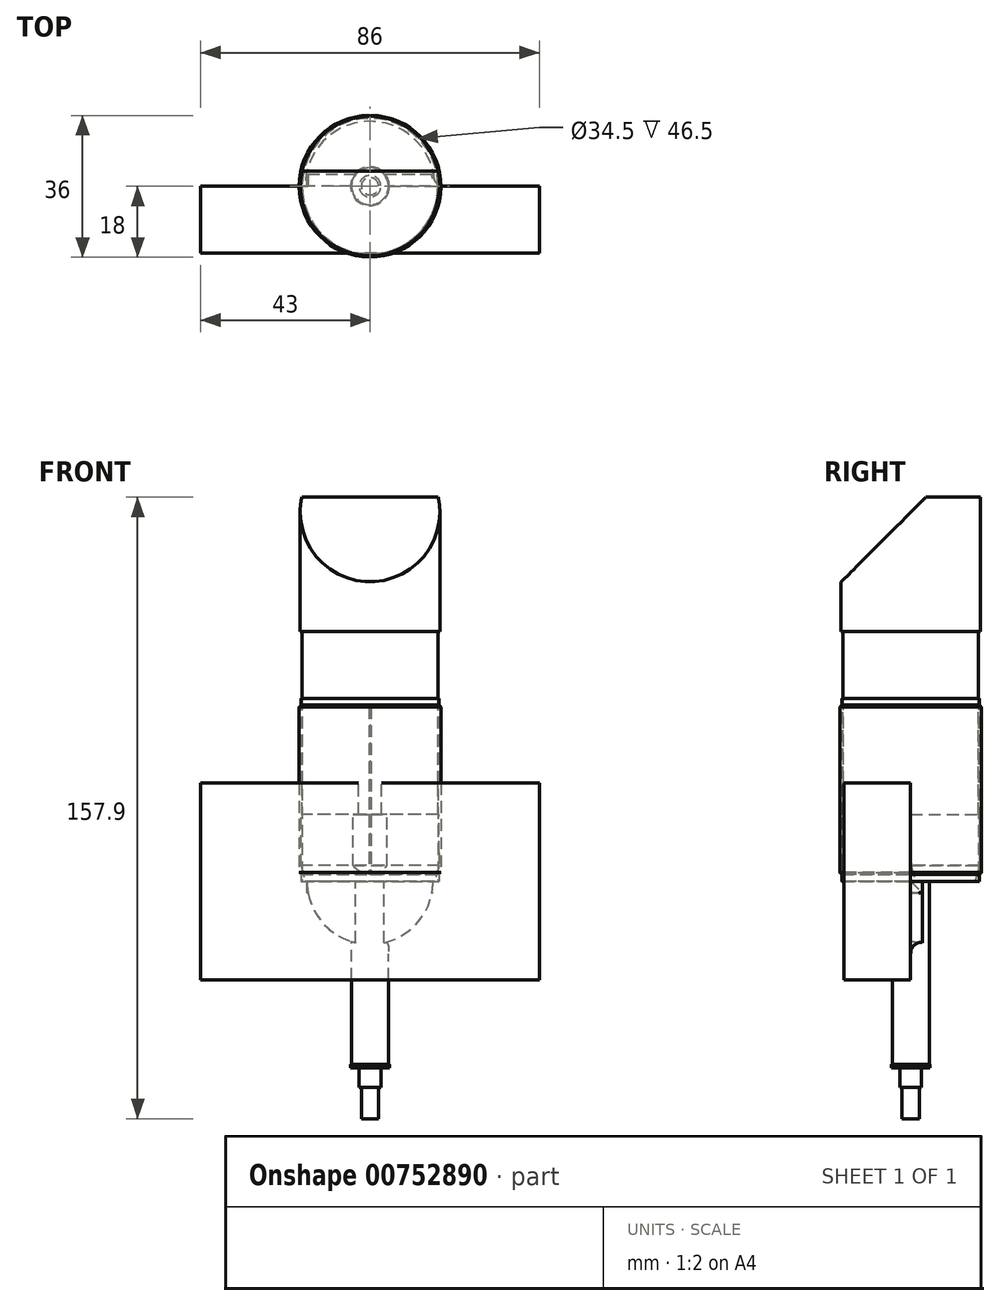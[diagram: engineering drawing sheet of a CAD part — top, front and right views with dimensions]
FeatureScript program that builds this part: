
annotation { "Feature Type Name" : "Feature", "Feature Type Description" : "" }
export const myFeature = defineFeature(function(context is Context, id is Id, definition is map)
    precondition{}
    {
        {
            var Q0;
            Q0=qCreatedBy(makeId("Front.planeOp"),FACE);
            var sketch = newSketch(context, id + "F0", { "sketchPlane" : qUnion([Q0])});
            skLineSegment(sketch, "E0.bottom", {"start": v(-4.7, 46.5) * mm, "end": v(4.7, 46.5) * mm, "construction": true});
            skLineSegment(sketch, "E0.top", {"start": v(-4.7, -46.5) * mm, "end": v(4.7, -46.5) * mm, "construction": true});
            skLineSegment(sketch, "E0.left", {"start": v(-4.7, 46.5) * mm, "end": v(-4.7, -46.5) * mm});
            skLineSegment(sketch, "E0.right", {"start": v(4.7, 46.5) * mm, "end": v(4.7, -46.5) * mm});
            skPoint(sketch, "E0.middle", {"position": v(0, 0) * mm});
            skLineSegment(sketch, "E1", {"start": v(-4.7, -46.5) * mm, "end": v(-4.92, -46.5) * mm});
            skLineSegment(sketch, "E2", {"start": v(-4.92, -46.5) * mm, "end": v(-4.92, -47.4) * mm});
            skLineSegment(sketch, "E3", {"start": v(-4.92, -47.4) * mm, "end": v(-2.75, -47.4) * mm});
            skLineSegment(sketch, "E4", {"start": v(0, 54.2) * mm, "end": v(0, -60.3) * mm});
            skLineSegment(sketch, "E5", {"start": v(-2.75, -47.4) * mm, "end": v(-2.75, -52.3) * mm});
            skLineSegment(sketch, "E6", {"start": v(-2.75, -52.3) * mm, "end": v(-2.2, -52.3) * mm});
            skLineSegment(sketch, "E7", {"start": v(-2.2, -52.3) * mm, "end": v(-2.2, -60.3) * mm});
            skLineSegment(sketch, "E8", {"start": v(-2.2, -60.3) * mm, "end": v(0, -60.3) * mm});
            skLineSegment(sketch, "E9.MirrorCS", {"start": v(2.2, -60.3) * mm, "end": v(0, -60.3) * mm});
            skLineSegment(sketch, "E10.MirrorCS", {"start": v(2.2, -52.3) * mm, "end": v(2.2, -60.3) * mm});
            skLineSegment(sketch, "E11.MirrorCS", {"start": v(2.75, -52.3) * mm, "end": v(2.2, -52.3) * mm});
            skLineSegment(sketch, "E12.MirrorCS", {"start": v(2.75, -47.4) * mm, "end": v(2.75, -52.3) * mm});
            skLineSegment(sketch, "E13.MirrorCS", {"start": v(4.93, -47.4) * mm, "end": v(2.75, -47.4) * mm});
            skLineSegment(sketch, "E14.MirrorCS", {"start": v(4.93, -46.5) * mm, "end": v(4.93, -47.4) * mm});
            skLineSegment(sketch, "E15.MirrorCS", {"start": v(4.7, -46.5) * mm, "end": v(4.93, -46.5) * mm});
            skLineSegment(sketch, "E16", {"start": v(-4.7, 46.5) * mm, "end": v(-4.92, 46.5) * mm});
            skLineSegment(sketch, "E17", {"start": v(-4.92, 46.5) * mm, "end": v(-4.92, 47.4) * mm});
            skLineSegment(sketch, "E18", {"start": v(-4.92, 47.4) * mm, "end": v(-2.4, 47.4) * mm});
            skLineSegment(sketch, "E19", {"start": v(-2.4, 47.4) * mm, "end": v(-2.4, 54.2) * mm});
            skLineSegment(sketch, "E20", {"start": v(-2.4, 54.2) * mm, "end": v(0, 54.2) * mm});
            skLineSegment(sketch, "E21.MirrorCS", {"start": v(2.4, 54.2) * mm, "end": v(0, 54.2) * mm});
            skLineSegment(sketch, "E22.MirrorCS", {"start": v(2.4, 47.4) * mm, "end": v(2.4, 54.2) * mm});
            skLineSegment(sketch, "E23.MirrorCS", {"start": v(4.92, 47.4) * mm, "end": v(2.4, 47.4) * mm});
            skLineSegment(sketch, "E24.MirrorCS", {"start": v(4.93, 46.5) * mm, "end": v(4.93, 47.4) * mm});
            skLineSegment(sketch, "E25.MirrorCS", {"start": v(4.7, 46.5) * mm, "end": v(4.92, 46.5) * mm});
            skSolve(sketch);
        }
        {
            var Q0;
            Q0=makeQuery(id+"F0.imprint","IMPRINT",FACE,{"disambiguationData":[TD([[makeQuery(id+"F0.imprint","IMPRINT",EDGE,{"derivedFrom":sQuery(id+"F0.wireOp",EDGE,"E0.left")}),1.0]])]});
            var Q1;
            Q1=sQuery(id+"F0.wireOp",EDGE,"E4");
            revolve(context, id + "F1", {"surfaceOperationType" : NewSurfaceOperationType.NEW, "entities" : qUnion([Q0]), "axis" : qUnion([Q1]), "revolveType" : RevolveType.FULL});
        }
        {
            var Q0;
            Q0=qCreatedBy(makeId("Front.planeOp"),FACE);
            var sketch = newSketch(context, id + "F2", { "sketchPlane" : qUnion([Q0])});
            skLineSegment(sketch, "E26", {"start": v(0, 0) * mm, "end": v(16.5, 0) * mm});
            skLineSegment(sketch, "E27", {"start": v(16.5, 0) * mm, "end": v(17.55, 4) * mm});
            skLineSegment(sketch, "E28", {"start": v(17.55, 4) * mm, "end": v(17.55, 17) * mm});
            skLineSegment(sketch, "E29", {"start": v(17.55, 17) * mm, "end": v(17.25, 17) * mm});
            skLineSegment(sketch, "E30", {"start": v(17.25, 17) * mm, "end": v(17.25, 63.5) * mm});
            skLineSegment(sketch, "E31", {"start": v(17.25, 63.5) * mm, "end": v(17.75, 63.5) * mm});
            skLineSegment(sketch, "E32", {"start": v(17.75, 63.5) * mm, "end": v(17.75, 97.6) * mm});
            skLineSegment(sketch, "E33", {"start": v(17.75, 97.6) * mm, "end": v(0, 97.6) * mm});
            skLineSegment(sketch, "E34", {"start": v(0, 97.6) * mm, "end": v(0, 0) * mm});
            skSolve(sketch);
        }
        {
            var Q0;
            Q0=makeQuery(id+"F2.imprint","IMPRINT",FACE,{"disambiguationData":[TD([[makeQuery(id+"F2.imprint","IMPRINT",EDGE,{"derivedFrom":sQuery(id+"F2.wireOp",EDGE,"E26")}),1.0]])]});
            var Q1;
            Q1=sQuery(id+"F2.wireOp",EDGE,"E34");
            revolve(context, id + "F3", {"surfaceOperationType" : NewSurfaceOperationType.NEW, "entities" : qUnion([Q0]), "axis" : qUnion([Q1]), "revolveType" : RevolveType.FULL});
        }
        {
            var Q0;
            Q0=qCreatedBy(makeId("Right.planeOp"),FACE);
            var sketch = newSketch(context, id + "F4", { "sketchPlane" : qUnion([Q0])});
            skLineSegment(sketch, "E35", {"start": v(-17.75, 63.5) * mm, "end": v(-17.75, 97.6) * mm, "construction": true});
            skLineSegment(sketch, "E36.0", {"start": v(-17.75, 97.6) * mm, "end": v(17.75, 97.6) * mm, "construction": true});
            skLineSegment(sketch, "E37", {"start": v(17.75, 97.6) * mm, "end": v(17.75, 63.5) * mm, "construction": true});
            skLineSegment(sketch, "E38.0", {"start": v(-17.75, 63.5) * mm, "end": v(17.75, 63.5) * mm, "construction": true});
            skLineSegment(sketch, "E39", {"start": v(-17.75, 97.6) * mm, "end": v(3.85, 97.6) * mm});
            skLineSegment(sketch, "E40", {"start": v(3.85, 97.6) * mm, "end": v(-17.75, 76) * mm});
            skLineSegment(sketch, "E41", {"start": v(-17.75, 76) * mm, "end": v(-17.75, 97.6) * mm});
            skLineSegment(sketch, "E42.0", {"start": v(-16.5, 0) * mm, "end": v(16.5, 0) * mm, "construction": true});
            skSolve(sketch);
        }
        {
            var Q0;
            Q0=makeQuery(id+"F4.imprint","IMPRINT",FACE,{"disambiguationData":[TD([[makeQuery(id+"F4.imprint","IMPRINT",EDGE,{"derivedFrom":sQuery(id+"F4.wireOp",EDGE,"E39")}),-1.0]])]});
            extrude(context, id + "F5", {"entities" : qUnion([Q0]), "operationType" : NewBodyOperationType.REMOVE, "endBound" : BoundingType.SYMMETRIC, "oppositeDirection" : true, "depth" : 50 * mm, "offsetDistance" : 25 * mm});
        }
        {
            var Q0;
            Q0=qCreatedBy(makeId("Front.planeOp"),FACE);
            var sketch = newSketch(context, id + "F6", { "sketchPlane" : qUnion([Q0])});
            skLineSegment(sketch, "E43", {"start": v(17.25, 46.5) * mm, "end": v(17.25, 0) * mm});
            skLineSegment(sketch, "E44", {"start": v(17.25, 0) * mm, "end": v(17.5, 0) * mm});
            skLineSegment(sketch, "E45", {"start": v(17.5, 0) * mm, "end": v(17.5, 1.75) * mm});
            skLineSegment(sketch, "E46", {"start": v(17.5, 1.75) * mm, "end": v(18, 1.75) * mm});
            skLineSegment(sketch, "E47", {"start": v(18, 1.75) * mm, "end": v(18, 44.75) * mm});
            skLineSegment(sketch, "E48", {"start": v(18, 44.75) * mm, "end": v(17.5, 44.75) * mm});
            skLineSegment(sketch, "E49", {"start": v(17.5, 44.75) * mm, "end": v(17.5, 46.5) * mm});
            skLineSegment(sketch, "E50", {"start": v(17.5, 46.5) * mm, "end": v(17.25, 46.5) * mm});
            skLineSegment(sketch, "E51", {"start": v(0, 1.24) * mm, "end": v(0, 39.4) * mm, "construction": true});
            skSolve(sketch);
        }
        {
            var Q0;
            Q0=makeQuery(id+"F6.imprint","IMPRINT",FACE,{"disambiguationData":[TD([[makeQuery(id+"F6.imprint","IMPRINT",EDGE,{"derivedFrom":sQuery(id+"F6.wireOp",EDGE,"E43")}),1.0]])]});
            var Q1;
            Q1=sQuery(id+"F6.wireOp",EDGE,"E51");
            revolve(context, id + "F7", {"surfaceOperationType" : NewSurfaceOperationType.NEW, "entities" : qUnion([Q0]), "axis" : qUnion([Q1]), "revolveType" : RevolveType.FULL});
        }
        {
            var Q0;
            Q0=makeQuery(id+"F7.opRevolve","SWEPT_EDGE",EDGE,{"disambiguationData":[OSD([sQuery(id+"F6.wireOp",EDGE,"E47"),sQuery(id+"F6.wireOp",EDGE,"E48")])]});
            var Q1;
            Q1=makeQuery(id+"F7.opRevolve","SWEPT_EDGE",EDGE,{"disambiguationData":[OSD([sQuery(id+"F6.wireOp",EDGE,"E46"),sQuery(id+"F6.wireOp",EDGE,"E47")])]});
            chamfer(context, id + "F8", {"entities" : qUnion([Q0, Q1]), "width" : 0.5 * mm, "tangentPropagation" : true});
        }
        {
            var Q0;
            Q0=qCreatedBy(makeId("Top.planeOp"),FACE);
            var sketch = newSketch(context, id + "F9", { "sketchPlane" : qUnion([Q0])});
            skLineSegment(sketch, "E52", {"start": v(0, 17.8) * mm, "end": v(-0.2, 18) * mm});
            skLineSegment(sketch, "E53", {"start": v(-0.2, 18) * mm, "end": v(0, 18) * mm});
            skLineSegment(sketch, "E54.MirrorCS", {"start": v(0.2, 18) * mm, "end": v(0, 18) * mm});
            skLineSegment(sketch, "E55.MirrorCS", {"start": v(0, 17.8) * mm, "end": v(0.2, 18) * mm});
            skCircle(sketch, "E56.0", {"center": v(0, 0) * mm, "radius": 18 * mm, "construction": true});
            skSolve(sketch);
        }
        {
            var Q0;
            Q0=makeQuery(id+"F9.imprint","IMPRINT",FACE,{"disambiguationData":[TD([[makeQuery(id+"F9.imprint","IMPRINT",EDGE,{"derivedFrom":sQuery(id+"F9.wireOp",EDGE,"E52")}),-1.0]])]});
            var Q1;
            Q1=makeQuery(id+"F7.opRevolve","SWEPT_FACE",FACE,{"disambiguationData":[OSD([sQuery(id+"F6.wireOp",EDGE,"E48")])]});
            extrude(context, id + "F10", {"entities" : qUnion([Q0]), "operationType" : NewBodyOperationType.REMOVE, "endBound" : BoundingType.THROUGH_ALL, "depth" : 25 * mm, "endBoundEntityFace" : qUnion([Q1]), "offsetDistance" : 25 * mm});
        }
        {
            var Q0;
            Q0=qCreatedBy(makeId("Front.planeOp"),FACE);
            var sketch = newSketch(context, id + "F11", { "sketchPlane" : qUnion([Q0])});
            skLineSegment(sketch, "E57.bottom", {"start": v(43, 25) * mm, "end": v(-43, 25) * mm});
            skLineSegment(sketch, "E57.top", {"start": v(43, -25) * mm, "end": v(-43, -25) * mm});
            skLineSegment(sketch, "E57.left", {"start": v(43, 25) * mm, "end": v(43, -25) * mm});
            skLineSegment(sketch, "E57.right", {"start": v(-43, 25) * mm, "end": v(-43, -25) * mm});
            skPoint(sketch, "E57.middle", {"position": v(0, 0) * mm});
            skSolve(sketch);
        }
        {
            var Q0;
            Q0=makeQuery(id+"F11.imprint","IMPRINT",FACE,{"disambiguationData":[TD([[makeQuery(id+"F11.imprint","IMPRINT",EDGE,{"derivedFrom":sQuery(id+"F11.wireOp",EDGE,"E57.bottom")}),1.0]])]});
            extrude(context, id + "F12", {"entities" : qUnion([Q0]), "depth" : 17 * mm, "offsetDistance" : 25 * mm});
        }
        {
            var Q0;
            Q0=makeQuery(id+"F12.opExtrude","CAP_FACE",FACE,{"disambiguationData":[OSD([sQuery(id+"F11.wireOp",EDGE,"E57.bottom"),sQuery(id+"F11.wireOp",EDGE,"E57.top"),sQuery(id+"F11.wireOp",EDGE,"E57.left"),sQuery(id+"F11.wireOp",EDGE,"E57.right")])],"isStart":true});
            var sketch = newSketch(context, id + "F13", { "sketchPlane" : qUnion([Q0])});
            skCircle(sketch, "E58", {"center": v(0, 0) * mm, "radius": 16 * mm});
            skSolve(sketch);
        }
        {
            var Q0;
            Q0=makeQuery(id+"F13.imprint","IMPRINT",FACE,{"disambiguationData":[TD([[makeQuery(id+"F13.imprint","IMPRINT",EDGE,{"derivedFrom":sQuery(id+"F13.wireOp",EDGE,"E58")}),1.0]])]});
            extrude(context, id + "F14", {"entities" : qUnion([Q0]), "operationType" : NewBodyOperationType.ADD, "depth" : 3 * mm, "offsetDistance" : 25 * mm});
        }
        {
            var Q0;
            Q0=makeQuery(id+"F14.opExtrude","CAP_EDGE",EDGE,{"disambiguationData":[OSD([sQuery(id+"F13.wireOp",EDGE,"E58")])],"isStart":true});
            fillet(context, id + "F15", {"entities" : qUnion([Q0]), "tangentPropagation" : true, "radius" : 3 * mm, "defaultsChanged" : true, "vertexSettings" : [], "allowEdgeOverflow" : false});
        }
        {
            var Q0;
            Q0=makeQuery(id+"F3.opRevolve","SWEPT_FACE",FACE,{"disambiguationData":[OSD([sQuery(id+"F2.wireOp",EDGE,"E26")])]});
            var sketch = newSketch(context, id + "F16", { "sketchPlane" : qUnion([Q0])});
            skCircle(sketch, "E59", {"center": v(0, 0) * mm, "radius": 16 * mm});
            skSolve(sketch);
        }
        {
            var Q0;
            Q0=makeQuery(id+"F16.imprint","IMPRINT",FACE,{"disambiguationData":[TD([[makeQuery(id+"F16.imprint","IMPRINT",EDGE,{"derivedFrom":sQuery(id+"F16.wireOp",EDGE,"E59")}),1.0]])]});
            extrude(context, id + "F17", {"entities" : qUnion([Q0]), "operationType" : NewBodyOperationType.ADD, "depth" : 3 * mm, "offsetDistance" : 25 * mm});
        }
    });
